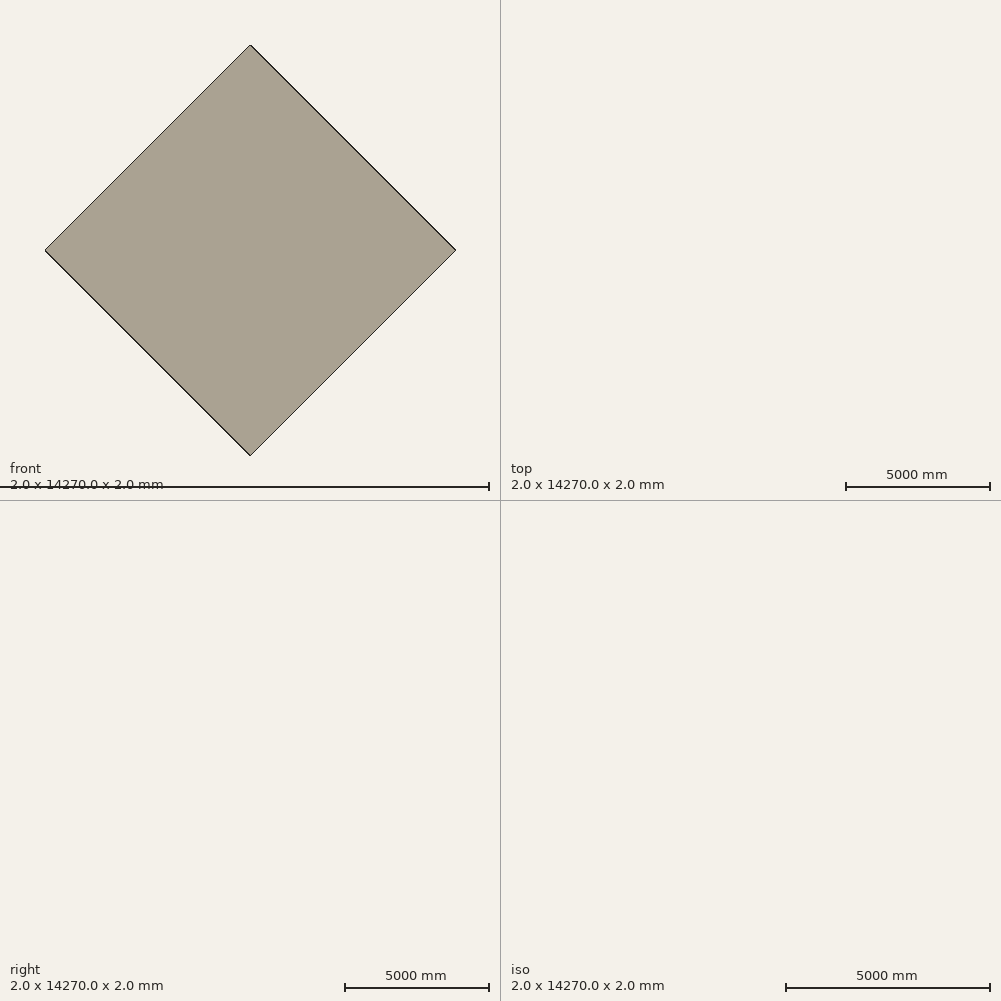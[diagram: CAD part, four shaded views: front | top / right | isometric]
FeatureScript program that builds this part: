
annotation { "Feature Type Name" : "Feature", "Feature Type Description" : "" }
export const myFeature = defineFeature(function(context is Context, id is Id, definition is map)
    precondition{}
    {
        {
            assignVariable(context, id + "F0", {"name" : "l", "anyValue" : 14270});
        }
        {
            var Q0;
            Q0=qCreatedBy(makeId("Front.planeOp"),FACE);
            var sketch = newSketch(context, id + "F1", { "sketchPlane" : qUnion([Q0])});
            skCircle(sketch, "E0", {"center": v(0, 0) * mm, "radius": 1 * mm});
            skSolve(sketch);
        }
        {
            var Q0;
            Q0=qSketchRegion(id+"F1",true);
            extrude(context, id + "F2", {"entities" : qUnion([Q0]), "depth" : (getVariable(context, 'l')) * mm, "offsetDistance" : 25 * mm});
        }
    });
